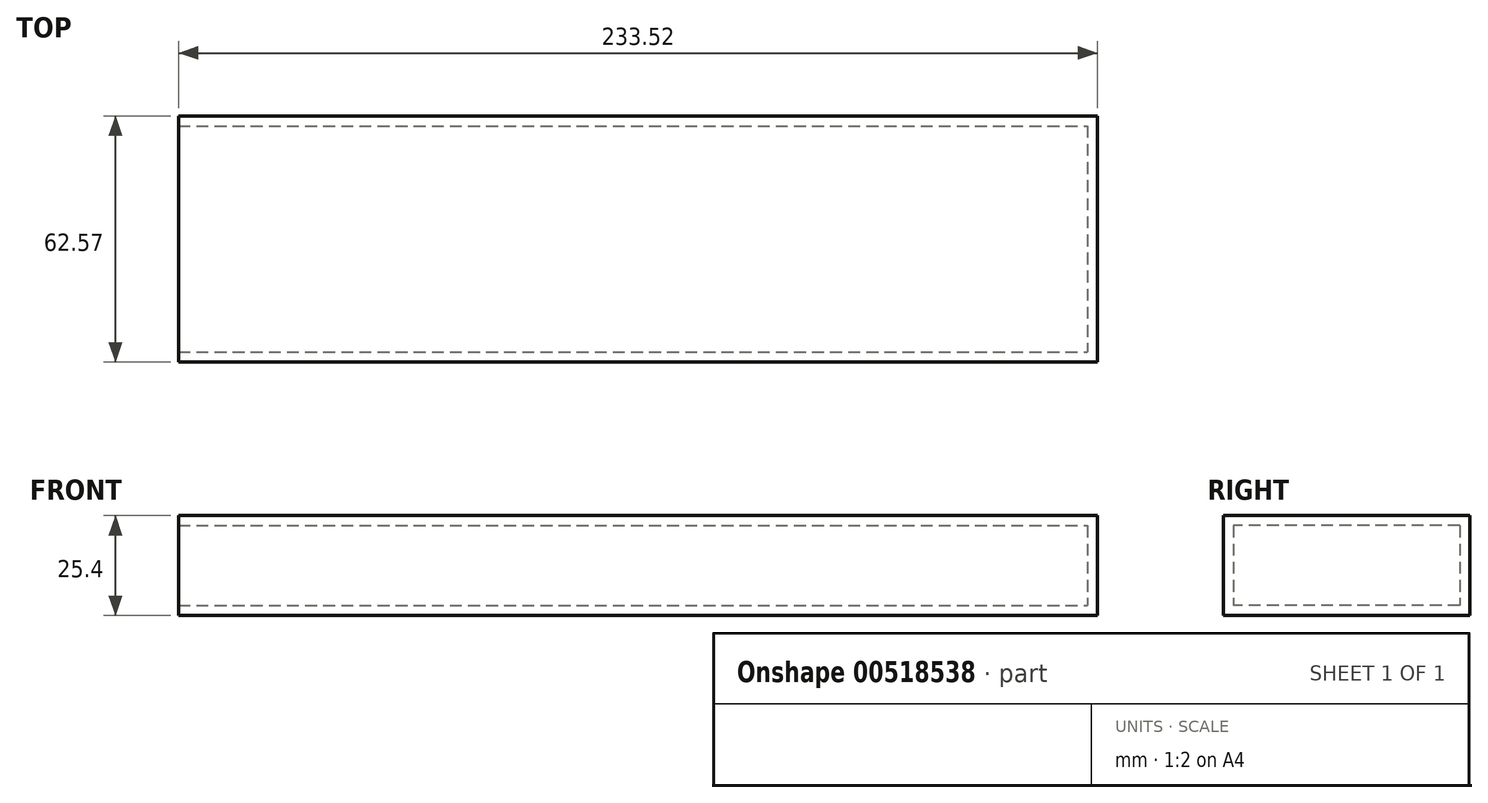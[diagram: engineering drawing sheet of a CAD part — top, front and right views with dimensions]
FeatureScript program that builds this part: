
annotation { "Feature Type Name" : "Feature", "Feature Type Description" : "" }
export const myFeature = defineFeature(function(context is Context, id is Id, definition is map)
    precondition{}
    {
        {
            var Q0;
            Q0=qCreatedBy(makeId("Top.planeOp"),FACE);
            var sketch = newSketch(context, id + "F0", { "sketchPlane" : qUnion([Q0])});
            skLineSegment(sketch, "E0.bottom", {"start": v(-126.57, 16.8) * mm, "end": v(106.95, 16.8) * mm});
            skLineSegment(sketch, "E0.top", {"start": v(-126.57, -45.78) * mm, "end": v(106.95, -45.78) * mm});
            skLineSegment(sketch, "E0.left", {"start": v(-126.57, 16.8) * mm, "end": v(-126.57, -45.78) * mm});
            skLineSegment(sketch, "E0.right", {"start": v(106.95, 16.8) * mm, "end": v(106.95, -45.78) * mm});
            skSolve(sketch);
        }
        {
            var Q0;
            Q0=makeQuery(id+"F0.imprint","IMPRINT",FACE,{"disambiguationData":[TD([[makeQuery(id+"F0.imprint","IMPRINT",EDGE,{"derivedFrom":sQuery(id+"F0.wireOp",EDGE,"E0.bottom")}),-1.0]])]});
            extrude(context, id + "F1", {"entities" : qUnion([Q0]), "depth" : 25.4 * mm, "offsetDistance" : 25.4 * mm});
        }
        {
            var Q0;
            Q0=makeQuery(id+"F1.opExtrude","SWEPT_FACE",FACE,{"disambiguationData":[OSD([sQuery(id+"F0.wireOp",EDGE,"E0.left")])]});
            shell(context, id + "F2", {"entities" : qUnion([Q0]), "thickness" : 2.54 * mm});
        }
    });
